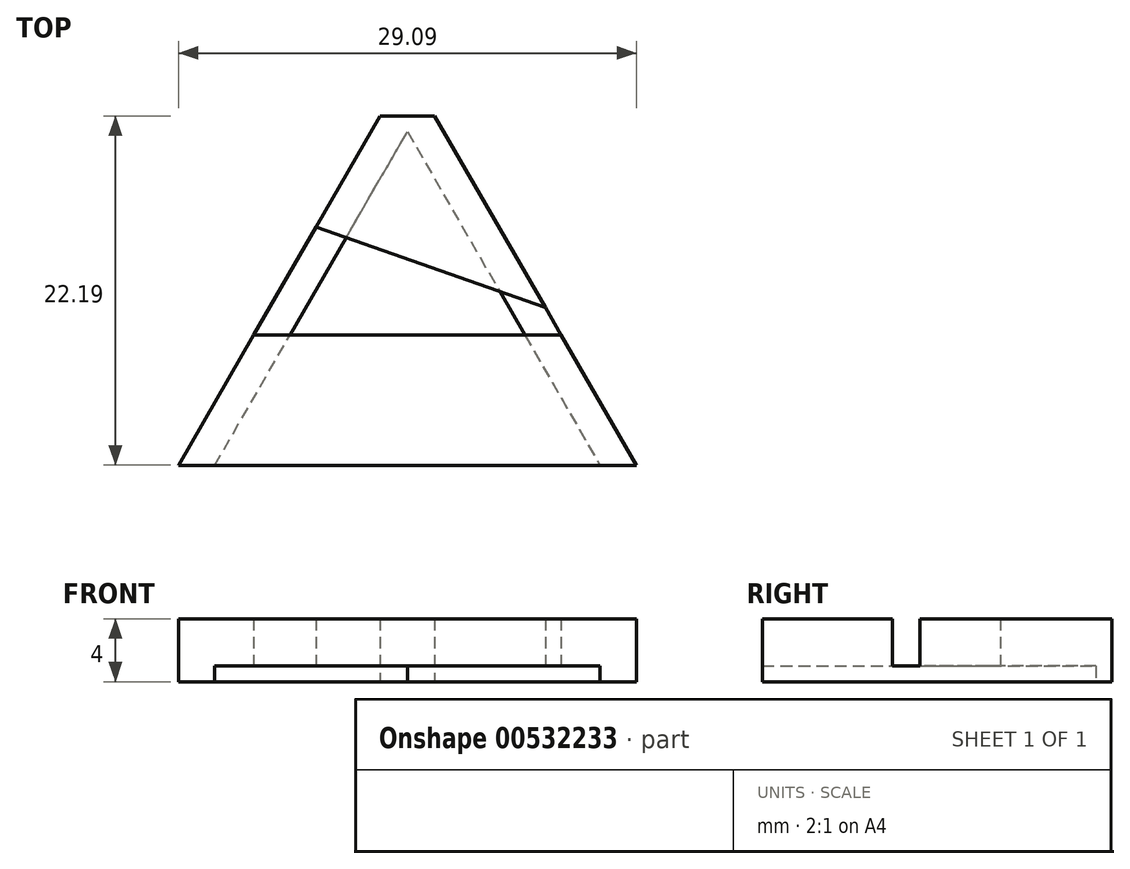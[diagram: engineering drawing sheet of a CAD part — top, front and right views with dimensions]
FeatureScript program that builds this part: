
annotation { "Feature Type Name" : "Feature", "Feature Type Description" : "" }
export const myFeature = defineFeature(function(context is Context, id is Id, definition is map)
    precondition{}
    {
        {
            var Q0;
            Q0=qCreatedBy(makeId("Top.planeOp"),FACE);
            var sketch = newSketch(context, id + "F0", { "sketchPlane" : qUnion([Q0])});
            skLineSegment(sketch, "E0", {"start": v(-15, -7.11) * mm, "end": v(-2.19, 15.08) * mm});
            skLineSegment(sketch, "E1", {"start": v(1.28, 15.08) * mm, "end": v(14.09, -7.11) * mm});
            skLineSegment(sketch, "E2.0", {"start": v(-0.46, 14.08) * mm, "end": v(11.78, -7.11) * mm});
            skLineSegment(sketch, "E2.1", {"start": v(-12.7, -7.11) * mm, "end": v(-0.46, 14.08) * mm});
            skLineSegment(sketch, "E3", {"start": v(-15, -7.11) * mm, "end": v(-12.7, -7.11) * mm});
            skLineSegment(sketch, "E4", {"start": v(14.09, -7.11) * mm, "end": v(11.78, -7.11) * mm});
            skLineSegment(sketch, "E5", {"start": v(-2.19, 15.08) * mm, "end": v(1.28, 15.08) * mm});
            skSolve(sketch);
        }
        {
            var Q0;
            Q0 = qSketchRegion(id + "F0", true);
            extrude(context, id + "F1", {"entities" : qUnion([Q0]), "depth" : 1 * mm, "offsetDistance" : 25 * mm});
        }
        {
            var Q0;
            Q0=makeQuery(id+"F1.opExtrude","CAP_FACE",FACE,{"disambiguationData":[OSD([sQuery(id+"F0.wireOp",EDGE,"E0"),sQuery(id+"F0.wireOp",EDGE,"E1"),sQuery(id+"F0.wireOp",EDGE,"E2.0"),sQuery(id+"F0.wireOp",EDGE,"E2.1"),sQuery(id+"F0.wireOp",EDGE,"E3"),sQuery(id+"F0.wireOp",EDGE,"E4")])],"isStart":false});
            var sketch = newSketch(context, id + "F2", { "sketchPlane" : qUnion([Q0])});
            skLineSegment(sketch, "E6", {"start": v(-15, -7.11) * mm, "end": v(-10.22, 1.16) * mm});
            skLineSegment(sketch, "E7", {"start": v(14.09, -7.11) * mm, "end": v(-15, -7.11) * mm});
            skLineSegment(sketch, "E8", {"start": v(-10.22, 1.16) * mm, "end": v(9.31, 1.16) * mm});
            skLineSegment(sketch, "E9.trimOffspring", {"start": v(9.31, 1.16) * mm, "end": v(14.09, -7.11) * mm});
            skLineSegment(sketch, "E10", {"start": v(-2.19, 15.08) * mm, "end": v(1.28, 15.08) * mm});
            skLineSegment(sketch, "E11", {"start": v(1.28, 15.08) * mm, "end": v(8.3, 2.9) * mm});
            skLineSegment(sketch, "E12", {"start": v(-2.19, 15.08) * mm, "end": v(-6.27, 8) * mm});
            skLineSegment(sketch, "E13", {"start": v(-6.27, 8) * mm, "end": v(8.3, 2.9) * mm});
            skSolve(sketch);
        }
        {
            var Q0;
            Q0 = qSketchRegion(id + "F2", true);
            extrude(context, id + "F3", {"entities" : qUnion([Q0]), "operationType" : NewBodyOperationType.ADD, "depth" : 3 * mm, "offsetDistance" : 25 * mm});
        }
    });
